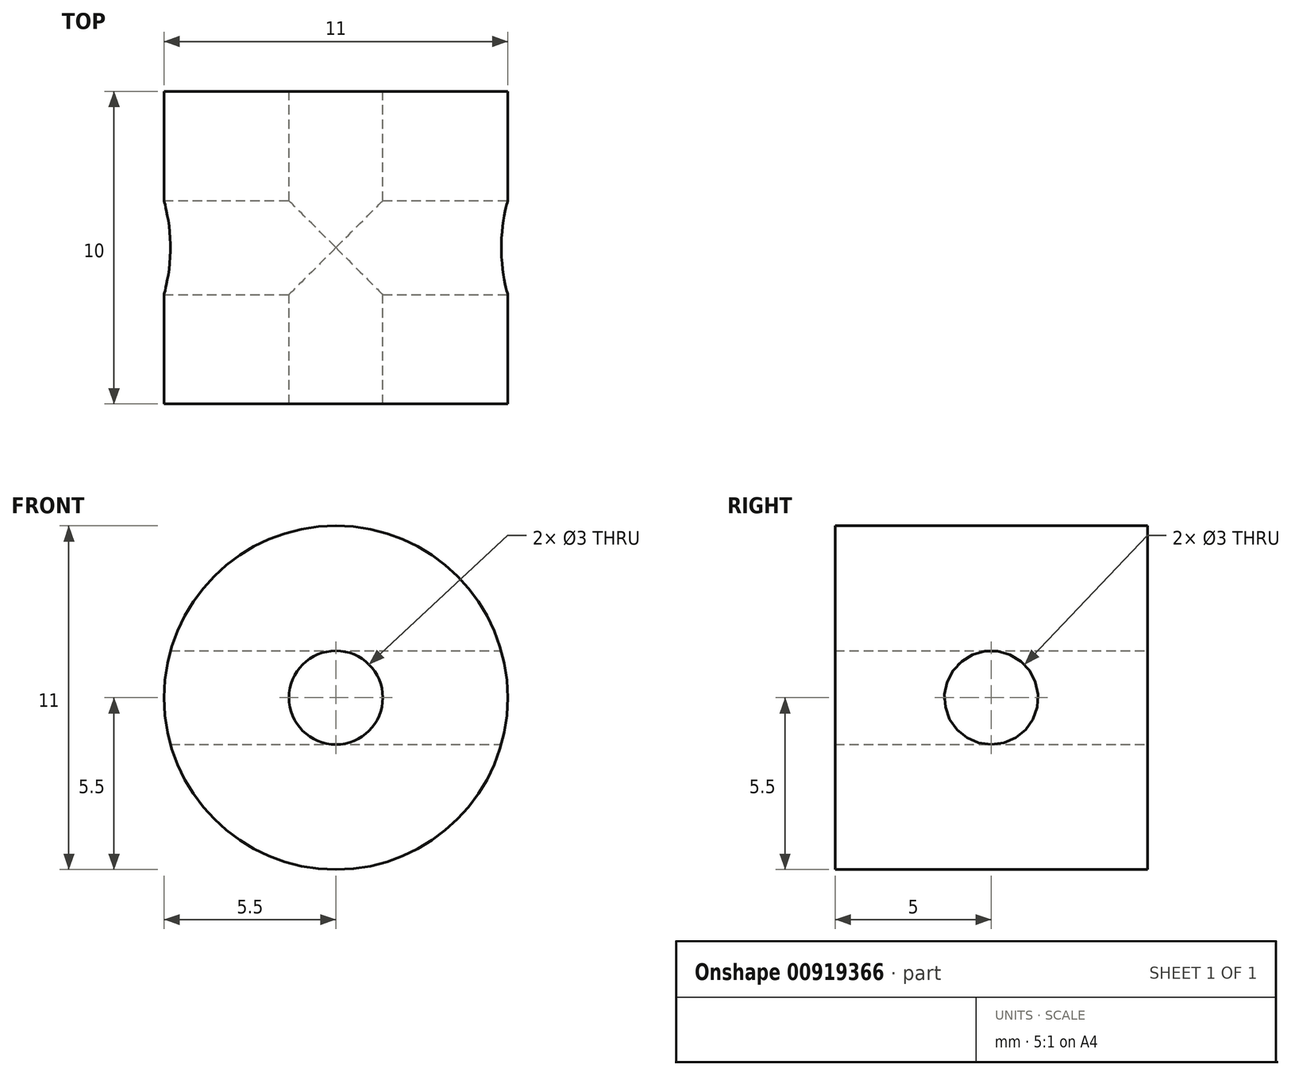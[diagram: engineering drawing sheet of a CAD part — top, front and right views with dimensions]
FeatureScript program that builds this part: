
annotation { "Feature Type Name" : "Feature", "Feature Type Description" : "" }
export const myFeature = defineFeature(function(context is Context, id is Id, definition is map)
    precondition{}
    {
        {
            var Q0;
            Q0=qCreatedBy(makeId("Top.planeOp"),FACE);
            var sketch = newSketch(context, id + "F0", { "sketchPlane" : qUnion([Q0])});
            skLineSegment(sketch, "E0", {"start": v(0, 30) * mm, "end": v(0, 0) * mm, "construction": true});
            skLineSegment(sketch, "E1.bottom", {"start": v(1.5, 0) * mm, "end": v(5.5, 0) * mm});
            skLineSegment(sketch, "E1.top", {"start": v(1.5, 10) * mm, "end": v(5.5, 10) * mm});
            skLineSegment(sketch, "E1.left", {"start": v(1.5, 0) * mm, "end": v(1.5, 10) * mm});
            skLineSegment(sketch, "E1.right", {"start": v(5.5, 0) * mm, "end": v(5.5, 10) * mm});
            skPoint(sketch, "E2", {"position": v(5.5, 5) * mm});
            skPoint(sketch, "E3", {"position": v(1.5, 5) * mm});
            skPoint(sketch, "E4", {"position": v(3.5, 10) * mm});
            skPoint(sketch, "E5", {"position": v(3.5, 0) * mm});
            skLineSegment(sketch, "E6.left", {"start": v(5.5, 6.5) * mm, "end": v(5.5, 3.5) * mm});
            skLineSegment(sketch, "E6.right", {"start": v(1.5, 6.5) * mm, "end": v(1.5, 3.5) * mm});
            skSolve(sketch);
        }
        {
            var Q0;
            {var subQ3=sQuery(id+"F0.wireOp",EDGE,"E1.bottom");Q0=makeQuery(id+"F0.imprint","IMPRINT",FACE,{"disambiguationData":[TD([[makeQuery(id+"F0.imprint","IMPRINT",EDGE,{"derivedFrom":subQ3}),1.0]])]});}
            var Q1;
            Q1=sQuery(id+"F0.wireOp",EDGE,"E0");
            revolve(context, id + "F1", {"surfaceOperationType" : NewSurfaceOperationType.NEW, "entities" : qUnion([Q0]), "axis" : qUnion([Q1]), "revolveType" : RevolveType.FULL});
        }
        {
            var Q0;
            Q0=makeQuery(id+"F1.opRevolve","SWEPT_FACE",FACE,{"disambiguationData":[OSD([sQuery(id+"F0.wireOp",EDGE,"E1.bottom")])]});
            cPlane(context, id + "F2", {"entities" : qUnion([Q0]), "cplaneType" : CPlaneType.OFFSET, "offset" : 5 * mm, "oppositeDirection" : true, "width" : 150 * mm, "height" : 150 * mm});
        }
        {
            var Q0;
            Q0=qCreatedBy(id+"F2.planeOp",FACE);
            var sketch = newSketch(context, id + "F3", { "sketchPlane" : qUnion([Q0])});
            skCircle(sketch, "E7.0", {"center": v(0, 0) * mm, "radius": 5.5 * mm, "construction": true});
            skLineSegment(sketch, "E8", {"start": v(0, 5.5) * mm, "end": v(0, -5.7) * mm, "construction": true});
            skLineSegment(sketch, "E9", {"start": v(0, 0) * mm, "end": v(5.5, 0) * mm, "construction": true});
            skPoint(sketch, "E10", {"position": v(5.5, 0) * mm});
            skPoint(sketch, "E11", {"position": v(0, 5.5) * mm});
            skSolve(sketch);
        }
        {
            var Q0;
            Q0=qCreatedBy(makeId("Right.planeOp"),FACE);
            var sketch = newSketch(context, id + "F4", { "sketchPlane" : qUnion([Q0])});
            skPoint(sketch, "E12.0", {"position": v(5, 0) * mm});
            skCircle(sketch, "E13", {"center": v(5, 0) * mm, "radius": 1.5 * mm});
            skSolve(sketch);
        }
        {
            var Q0;
            Q0 = qSketchRegion(id + "F4", true);
            extrude(context, id + "F5", {"entities" : qUnion([Q0]), "operationType" : NewBodyOperationType.REMOVE, "endBound" : BoundingType.SYMMETRIC, "oppositeDirection" : true, "depth" : 25 * mm, "offsetDistance" : 25 * mm});
        }
    });
